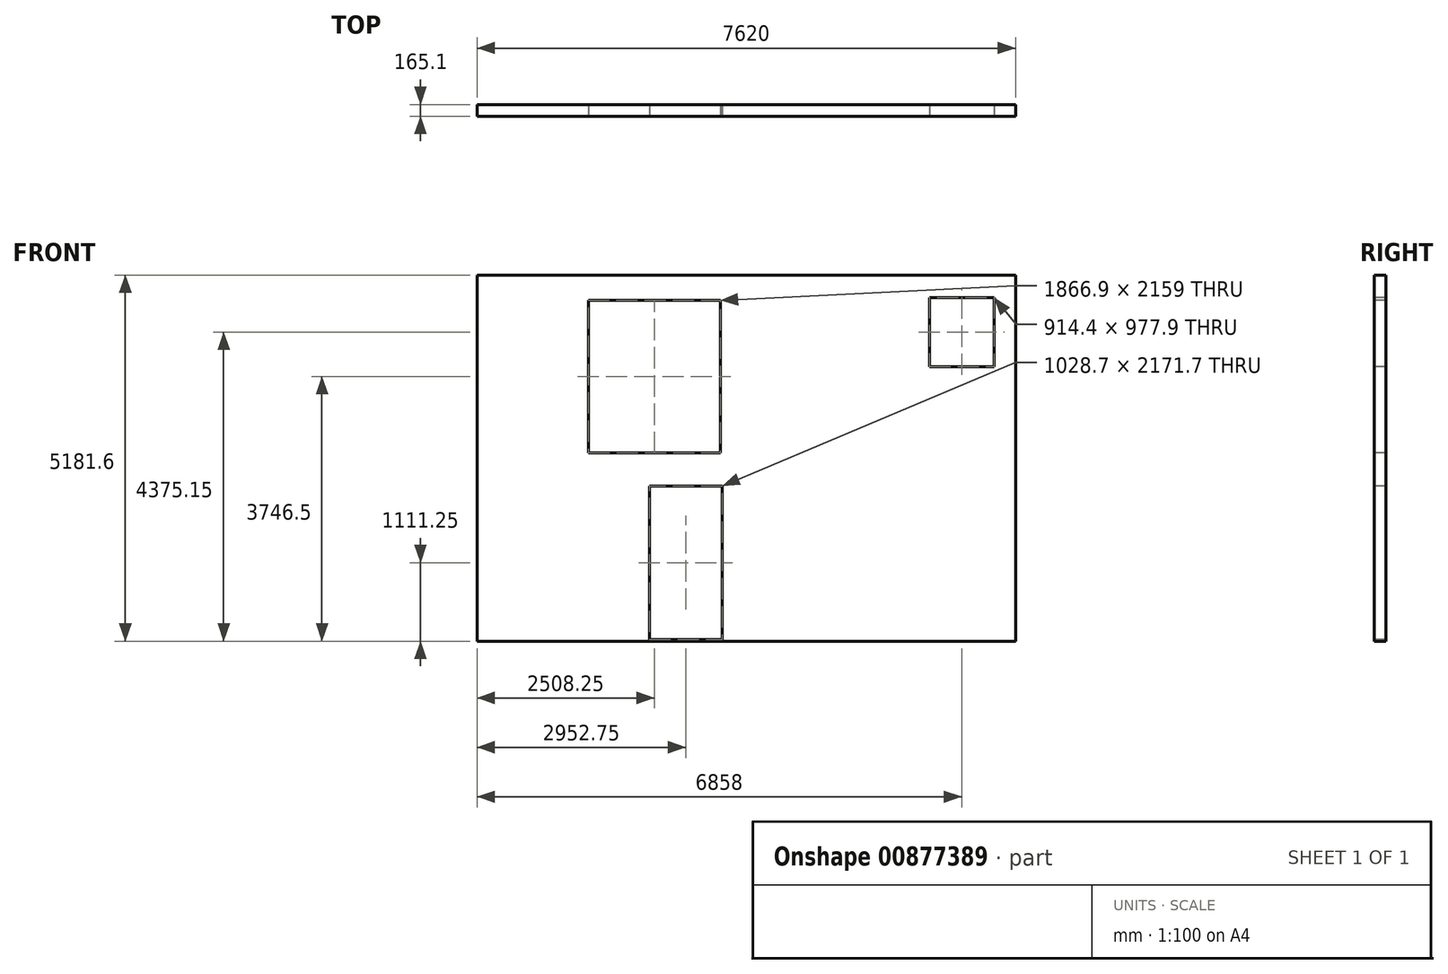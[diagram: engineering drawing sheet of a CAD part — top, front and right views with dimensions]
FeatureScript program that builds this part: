
annotation { "Feature Type Name" : "Feature", "Feature Type Description" : "" }
export const myFeature = defineFeature(function(context is Context, id is Id, definition is map)
    precondition{}
    {
        {
            var Q0;
            Q0=qCreatedBy(makeId("Front.planeOp"),FACE);
            var sketch = newSketch(context, id + "F0", { "sketchPlane" : qUnion([Q0])});
            skLineSegment(sketch, "E0.bottom", {"start": v(-5052.4, 2745.93) * mm, "end": v(2567.6, 2745.93) * mm});
            skLineSegment(sketch, "E0.top", {"start": v(-5052.4, -2435.67) * mm, "end": v(2567.6, -2435.67) * mm});
            skLineSegment(sketch, "E0.left", {"start": v(-5052.4, 2745.93) * mm, "end": v(-5052.4, -2435.67) * mm});
            skLineSegment(sketch, "E0.right", {"start": v(2567.6, 2745.93) * mm, "end": v(2567.6, -2435.67) * mm});
            skSolve(sketch);
        }
        {
            var Q0;
            Q0=makeQuery(id+"F0.imprint","IMPRINT",FACE,{"disambiguationData":[TD([[makeQuery(id+"F0.imprint","IMPRINT",EDGE,{"derivedFrom":sQuery(id+"F0.wireOp",EDGE,"E0.bottom")}),-1.0]])]});
            extrude(context, id + "F1", {"entities" : qUnion([Q0]), "depth" : 165.1 * mm, "offsetDistance" : 25.4 * mm});
        }
        {
            var Q0;
            Q0=makeQuery(id+"F1.opExtrude","CAP_FACE",FACE,{"disambiguationData":[OSD([sQuery(id+"F0.wireOp",EDGE,"E0.bottom"),sQuery(id+"F0.wireOp",EDGE,"E0.top"),sQuery(id+"F0.wireOp",EDGE,"E0.left"),sQuery(id+"F0.wireOp",EDGE,"E0.right")])],"isStart":false});
            var sketch = newSketch(context, id + "F2", { "sketchPlane" : qUnion([Q0])});
            skLineSegment(sketch, "E1.bottom", {"start": v(-3477.6, 2390.33) * mm, "end": v(-1610.7, 2390.33) * mm});
            skLineSegment(sketch, "E1.top", {"start": v(-3477.6, 231.33) * mm, "end": v(-1610.7, 231.33) * mm});
            skLineSegment(sketch, "E1.left", {"start": v(-3477.6, 2390.33) * mm, "end": v(-3477.6, 231.33) * mm});
            skLineSegment(sketch, "E1.right", {"start": v(-1610.7, 2390.33) * mm, "end": v(-1610.7, 231.33) * mm});
            skSolve(sketch);
        }
        {
            var Q0;
            Q0 = qSketchRegion(id + "F2", true);
            extrude(context, id + "F3", {"entities" : qUnion([Q0]), "operationType" : NewBodyOperationType.REMOVE, "endBound" : BoundingType.THROUGH_ALL, "oppositeDirection" : true, "depth" : 25.4 * mm, "offsetDistance" : 25.4 * mm});
        }
        {
            var Q0;
            Q0=makeQuery(id+"F1.opExtrude","CAP_FACE",FACE,{"disambiguationData":[OSD([sQuery(id+"F0.wireOp",EDGE,"E0.bottom"),sQuery(id+"F0.wireOp",EDGE,"E0.top"),sQuery(id+"F0.wireOp",EDGE,"E0.left"),sQuery(id+"F0.wireOp",EDGE,"E0.right")])],"isStart":false});
            var sketch = newSketch(context, id + "F4", { "sketchPlane" : qUnion([Q0])});
            skLineSegment(sketch, "E2.bottom", {"start": v(1348.4, 2428.43) * mm, "end": v(2262.8, 2428.43) * mm});
            skLineSegment(sketch, "E2.top", {"start": v(1348.4, 1450.53) * mm, "end": v(2262.8, 1450.53) * mm});
            skLineSegment(sketch, "E2.left", {"start": v(1348.4, 2428.43) * mm, "end": v(1348.4, 1450.53) * mm});
            skLineSegment(sketch, "E2.right", {"start": v(2262.8, 2428.43) * mm, "end": v(2262.8, 1450.53) * mm});
            skSolve(sketch);
        }
        {
            var Q0;
            Q0=makeQuery(id+"F4.imprint","IMPRINT",FACE,{"disambiguationData":[TD([[makeQuery(id+"F4.imprint","IMPRINT",EDGE,{"derivedFrom":sQuery(id+"F4.wireOp",EDGE,"E2.bottom")}),-1.0]])]});
            extrude(context, id + "F5", {"entities" : qUnion([Q0]), "operationType" : NewBodyOperationType.REMOVE, "endBound" : BoundingType.THROUGH_ALL, "oppositeDirection" : true, "depth" : 25.4 * mm, "offsetDistance" : 25.4 * mm});
        }
        {
            var Q0;
            Q0=makeQuery(id+"F1.opExtrude","CAP_FACE",FACE,{"disambiguationData":[OSD([sQuery(id+"F0.wireOp",EDGE,"E0.bottom"),sQuery(id+"F0.wireOp",EDGE,"E0.top"),sQuery(id+"F0.wireOp",EDGE,"E0.left"),sQuery(id+"F0.wireOp",EDGE,"E0.right")])],"isStart":false});
            var sketch = newSketch(context, id + "F6", { "sketchPlane" : qUnion([Q0])});
            skLineSegment(sketch, "E3.bottom", {"start": v(-2614, -238.57) * mm, "end": v(-1585.3, -238.57) * mm});
            skLineSegment(sketch, "E3.top", {"start": v(-2614, -2410.27) * mm, "end": v(-1585.3, -2410.27) * mm});
            skLineSegment(sketch, "E3.left", {"start": v(-2614, -238.57) * mm, "end": v(-2614, -2410.27) * mm});
            skLineSegment(sketch, "E3.right", {"start": v(-1585.3, -238.57) * mm, "end": v(-1585.3, -2410.27) * mm});
            skSolve(sketch);
        }
        {
            var Q0;
            Q0=makeQuery(id+"F6.imprint","IMPRINT",FACE,{"disambiguationData":[TD([[makeQuery(id+"F6.imprint","IMPRINT",EDGE,{"derivedFrom":sQuery(id+"F6.wireOp",EDGE,"E3.bottom")}),-1.0]])]});
            extrude(context, id + "F7", {"entities" : qUnion([Q0]), "operationType" : NewBodyOperationType.REMOVE, "endBound" : BoundingType.THROUGH_ALL, "oppositeDirection" : true, "depth" : 25.4 * mm, "offsetDistance" : 25.4 * mm});
        }
    });
